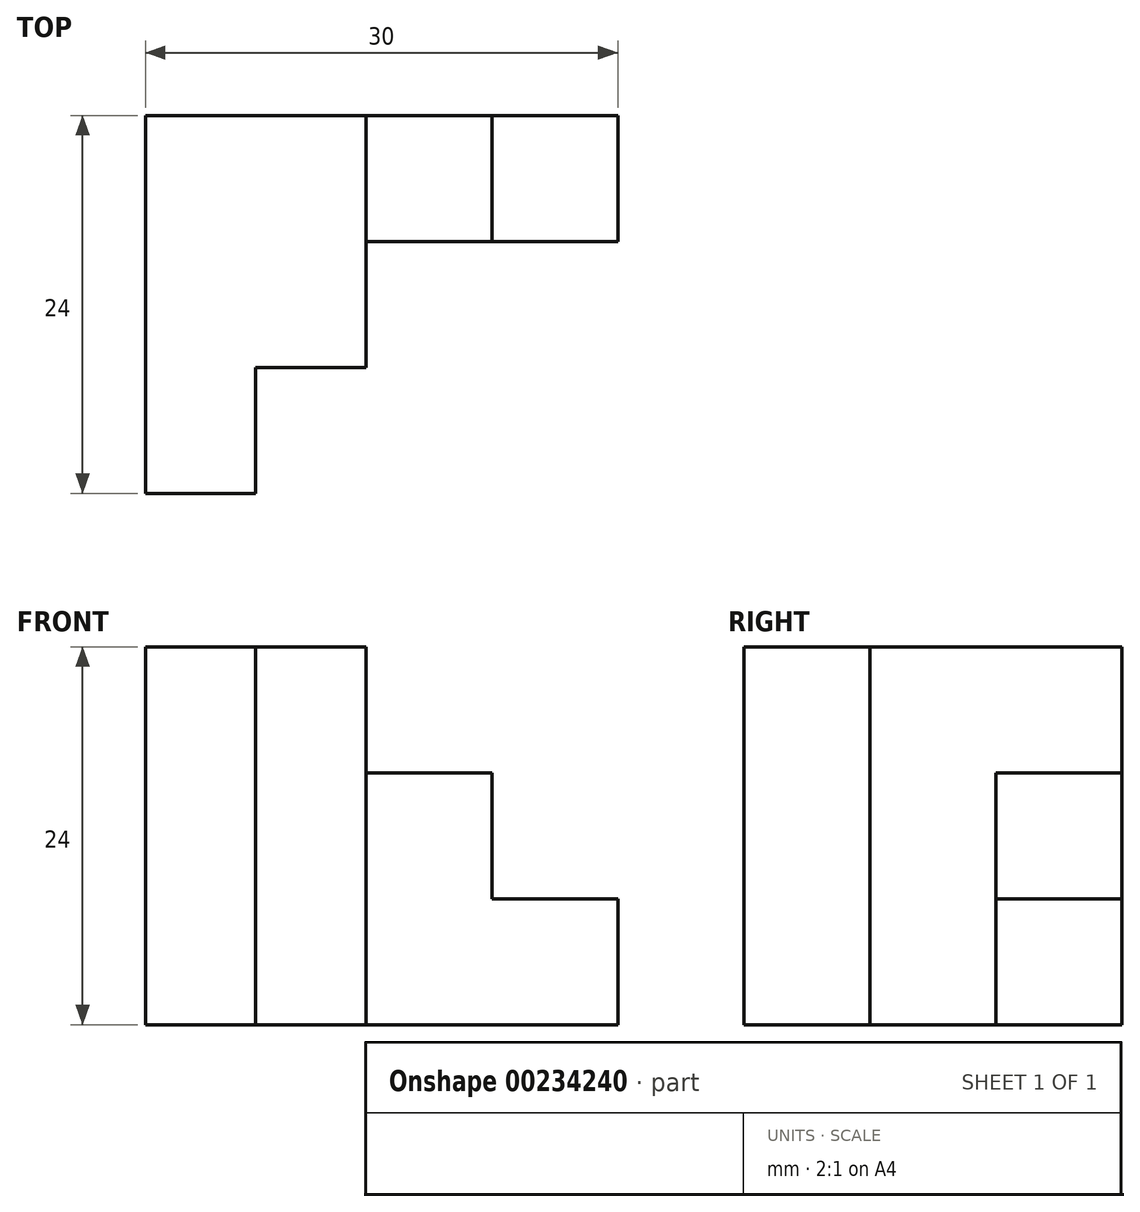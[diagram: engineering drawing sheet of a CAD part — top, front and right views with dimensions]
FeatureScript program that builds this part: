
annotation { "Feature Type Name" : "Feature", "Feature Type Description" : "" }
export const myFeature = defineFeature(function(context is Context, id is Id, definition is map)
    precondition{}
    {
        {
            var Q0;
            Q0=qCreatedBy(makeId("Top.planeOp"),FACE);
            var sketch = newSketch(context, id + "F0", { "sketchPlane" : qUnion([Q0])});
            skLineSegment(sketch, "E0", {"start": v(0, 0) * mm, "end": v(0, 24) * mm});
            skLineSegment(sketch, "E1", {"start": v(0, 0) * mm, "end": v(7, 0) * mm});
            skLineSegment(sketch, "E2", {"start": v(7, 0) * mm, "end": v(7, 8) * mm});
            skLineSegment(sketch, "E3", {"start": v(7, 8) * mm, "end": v(14, 8) * mm});
            skLineSegment(sketch, "E4", {"start": v(14, 8) * mm, "end": v(14, 24) * mm});
            skLineSegment(sketch, "E5", {"start": v(0, 24) * mm, "end": v(14, 24) * mm});
            skLineSegment(sketch, "E6", {"start": v(0, 0) * mm, "end": v(30, 0) * mm});
            skPoint(sketch, "E7", {"position": v(14, 16) * mm});
            skLineSegment(sketch, "E8", {"start": v(14, 16) * mm, "end": v(22, 16) * mm});
            skLineSegment(sketch, "E9", {"start": v(22, 16) * mm, "end": v(22, 24) * mm});
            skLineSegment(sketch, "E10", {"start": v(14, 24) * mm, "end": v(22, 24) * mm});
            skLineSegment(sketch, "E11", {"start": v(22, 16) * mm, "end": v(30, 16) * mm});
            skLineSegment(sketch, "E12", {"start": v(30, 16) * mm, "end": v(30, 24) * mm});
            skLineSegment(sketch, "E13", {"start": v(30, 24) * mm, "end": v(22, 24) * mm});
            skSolve(sketch);
        }
        {
            var Q0;
            {var subQ4=sQuery(id+"F0.wireOp",EDGE,"E0");Q0=makeQuery(id+"F0.imprint","IMPRINT",FACE,{"disambiguationData":[TD([[makeQuery(id+"F0.imprint","IMPRINT",EDGE,{"derivedFrom":subQ4}),-1.0]])]});}
            extrude(context, id + "F1", {"entities" : qUnion([Q0]), "depth" : 24 * mm});
        }
        {
            var Q0;
            {var subQ2=sQuery(id+"F0.wireOp",EDGE,"E8");Q0=makeQuery(id+"F0.imprint","IMPRINT",FACE,{"disambiguationData":[TD([[makeQuery(id+"F0.imprint","IMPRINT",EDGE,{"derivedFrom":subQ2}),1.0]])]});}
            extrude(context, id + "F2", {"entities" : qUnion([Q0]), "operationType" : NewBodyOperationType.ADD, "depth" : 16 * mm});
        }
        {
            var Q0;
            Q0=makeQuery(id+"F0.imprint","IMPRINT",FACE,{"disambiguationData":[TD([[makeQuery(id+"F0.imprint","IMPRINT",EDGE,{"derivedFrom":sQuery(id+"F0.wireOp",EDGE,"E9")}),-1.0]])]});
            extrude(context, id + "F3", {"entities" : qUnion([Q0]), "operationType" : NewBodyOperationType.ADD, "depth" : 8 * mm});
        }
    });
